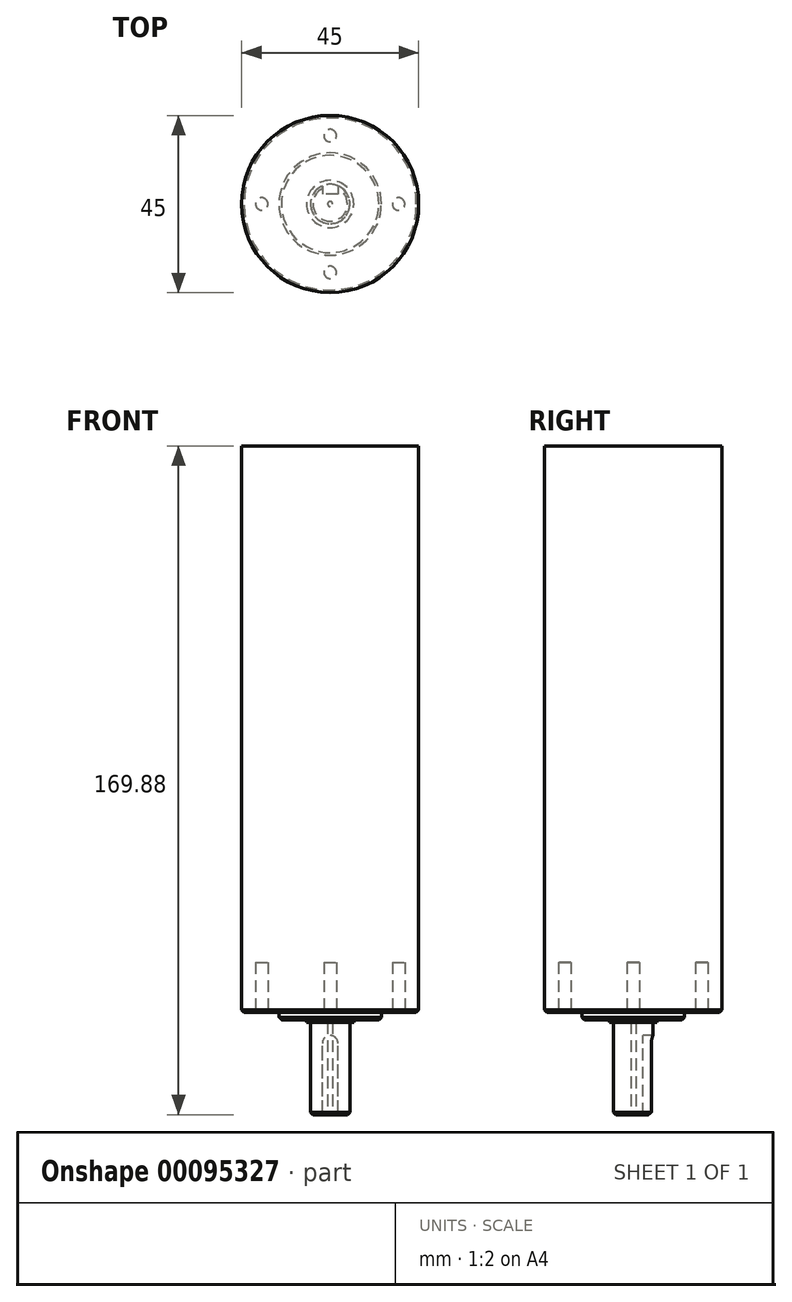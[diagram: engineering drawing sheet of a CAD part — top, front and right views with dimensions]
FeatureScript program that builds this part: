
annotation { "Feature Type Name" : "Feature", "Feature Type Description" : "" }
export const myFeature = defineFeature(function(context is Context, id is Id, definition is map)
    precondition{}
    {
        {
            var Q0;
            Q0=qCreatedBy(makeId("Top.planeOp"),FACE);
            var sketch = newSketch(context, id + "F0", { "sketchPlane" : qUnion([Q0])});
            skCircle(sketch, "E0", {"center": v(0, 0) * mm, "radius": 22.5 * mm});
            skSolve(sketch);
        }
        {
            var Q0;
            Q0=makeQuery(id+"F0.imprint","IMPRINT",FACE,{"disambiguationData":[TD([[makeQuery(id+"F0.imprint","IMPRINT",EDGE,{"derivedFrom":sQuery(id+"F0.wireOp",EDGE,"E0")}),1.0]])]});
            extrude(context, id + "F1", {"entities" : qUnion([Q0]), "oppositeDirection" : true, "depth" : 143.84 * mm});
        }
        {
            var Q0;
            Q0=makeQuery(id+"F1.opExtrude","CAP_FACE",FACE,{"disambiguationData":[OSD([sQuery(id+"F0.wireOp",EDGE,"E0")])],"isStart":false});
            var sketch = newSketch(context, id + "F2", { "sketchPlane" : qUnion([Q0])});
            skCircle(sketch, "E1", {"center": v(0, 0) * mm, "radius": 13 * mm});
            skSolve(sketch);
        }
        {
            var Q0;
            Q0=makeQuery(id+"F2.imprint","IMPRINT",FACE,{"disambiguationData":[TD([[makeQuery(id+"F2.imprint","IMPRINT",EDGE,{"derivedFrom":sQuery(id+"F2.wireOp",EDGE,"E1")}),1.0]])]});
            extrude(context, id + "F3", {"entities" : qUnion([Q0]), "operationType" : NewBodyOperationType.ADD, "depth" : 1.9 * mm});
        }
        {
            var Q0;
            Q0=makeQuery(id+"F3.opExtrude","CAP_FACE",FACE,{"disambiguationData":[OSD([sQuery(id+"F2.wireOp",EDGE,"E1")])],"isStart":false});
            var sketch = newSketch(context, id + "F4", { "sketchPlane" : qUnion([Q0])});
            skCircle(sketch, "E2", {"center": v(0, 0) * mm, "radius": 6 * mm});
            skSolve(sketch);
        }
        {
            var Q0;
            Q0=makeQuery(id+"F4.imprint","IMPRINT",FACE,{"disambiguationData":[TD([[makeQuery(id+"F4.imprint","IMPRINT",EDGE,{"derivedFrom":sQuery(id+"F4.wireOp",EDGE,"E2")}),1.0]])]});
            extrude(context, id + "F5", {"entities" : qUnion([Q0]), "operationType" : NewBodyOperationType.ADD, "depth" : 0.64 * mm});
        }
        {
            var Q0;
            Q0=makeQuery(id+"F5.opExtrude","CAP_FACE",FACE,{"disambiguationData":[OSD([sQuery(id+"F4.wireOp",EDGE,"E2")])],"isStart":false});
            var sketch = newSketch(context, id + "F6", { "sketchPlane" : qUnion([Q0])});
            skCircle(sketch, "E3", {"center": v(0, 0) * mm, "radius": 5 * mm});
            skSolve(sketch);
        }
        {
            var Q0;
            Q0=makeQuery(id+"F6.imprint","IMPRINT",FACE,{"disambiguationData":[TD([[makeQuery(id+"F6.imprint","IMPRINT",EDGE,{"derivedFrom":sQuery(id+"F6.wireOp",EDGE,"E3")}),1.0]])]});
            extrude(context, id + "F7", {"entities" : qUnion([Q0]), "operationType" : NewBodyOperationType.ADD, "depth" : 23.5 * mm});
        }
        {
            var Q0;
            Q0=qCreatedBy(makeId("Front.planeOp"),FACE);
            cPlane(context, id + "F8", {"entities" : qUnion([Q0]), "cplaneType" : CPlaneType.OFFSET, "offset" : 2.45 * mm, "oppositeDirection" : true, "width" : 152.4 * mm, "height" : 152.4 * mm});
        }
        {
            var Q0;
            Q0=qCreatedBy(id+"F8.planeOp",FACE);
            var sketch = newSketch(context, id + "F9", { "sketchPlane" : qUnion([Q0])});
            skLineSegment(sketch, "E4", {"start": v(5, -146.38) * mm, "end": v(5, -169.88) * mm, "construction": true});
            skLineSegment(sketch, "E5", {"start": v(-5, -169.88) * mm, "end": v(-5, -146.38) * mm, "construction": true});
            skLineSegment(sketch, "E6", {"start": v(0, -169.88) * mm, "end": v(-1.98, -169.88) * mm});
            skLineSegment(sketch, "E7", {"start": v(-1.98, -169.88) * mm, "end": v(-1.98, -151.74) * mm});
            skLineSegment(sketch, "E8", {"start": v(0, -169.88) * mm, "end": v(0, -146.38) * mm, "construction": true});
            skLineSegment(sketch, "E9.MirrorCS", {"start": v(1.98, -169.88) * mm, "end": v(1.98, -151.74) * mm});
            skLineSegment(sketch, "E10.MirrorCS", {"start": v(0, -169.88) * mm, "end": v(1.98, -169.88) * mm});
            skArc(sketch, "E11", {"start": v(1.98, -151.74) * mm, "mid": v(0, -149.76) * mm, "end": v(-1.98, -151.74) * mm});
            skSolve(sketch);
        }
        {
            var Q0;
            Q0 = qSketchRegion(id + "F9", true);
            extrude(context, id + "F10", {"entities" : qUnion([Q0]), "operationType" : NewBodyOperationType.REMOVE, "endBound" : BoundingType.THROUGH_ALL, "oppositeDirection" : true, "depth" : 25.4 * mm});
        }
        {
            var Q0;
            Q0=makeQuery(id+"F7.opExtrude","CAP_FACE",FACE,{"disambiguationData":[OSD([sQuery(id+"F6.wireOp",EDGE,"E3")])],"isStart":false});
            var sketch = newSketch(context, id + "F11", { "sketchPlane" : qUnion([Q0])});
            skCircle(sketch, "E12", {"center": v(0, 0) * mm, "radius": 0.64 * mm});
            skSolve(sketch);
        }
        {
            var Q0;
            Q0=makeQuery(id+"F11.imprint","IMPRINT",FACE,{"disambiguationData":[TD([[makeQuery(id+"F11.imprint","IMPRINT",EDGE,{"derivedFrom":sQuery(id+"F11.wireOp",EDGE,"E12")}),1.0]])]});
            extrude(context, id + "F12", {"entities" : qUnion([Q0]), "operationType" : NewBodyOperationType.REMOVE, "oppositeDirection" : true, "depth" : 23.5 * mm});
        }
        {
            var Q0;
            Q0=makeQuery(id+"F1.opExtrude","CAP_FACE",FACE,{"disambiguationData":[OSD([sQuery(id+"F0.wireOp",EDGE,"E0")])],"isStart":false});
            var sketch = newSketch(context, id + "F13", { "sketchPlane" : qUnion([Q0])});
            skLineSegment(sketch, "E13", {"start": v(0, 0) * mm, "end": v(0, 22.5) * mm, "construction": true});
            skCircle(sketch, "E14", {"center": v(0, 17.38) * mm, "radius": 1.59 * mm});
            skCircle(sketch, "E15.1.0", {"center": v(-17.38, 0) * mm, "radius": 1.59 * mm});
            skCircle(sketch, "E15.2.0", {"center": v(0, -17.38) * mm, "radius": 1.59 * mm});
            skCircle(sketch, "E15.3.0", {"center": v(17.38, 0) * mm, "radius": 1.59 * mm});
            skPoint(sketch, "E15.center", {"position": v(0, 0) * mm});
            skSolve(sketch);
        }
        {
            var Q0;
            Q0 = qSketchRegion(id + "F13", true);
            extrude(context, id + "F14", {"entities" : qUnion([Q0]), "operationType" : NewBodyOperationType.REMOVE, "oppositeDirection" : true, "depth" : 12.7 * mm});
        }
        {
            var Q0;
            Q0=makeQuery(id+"F12.boolean.opBoolean","COPY",EDGE,{"derivedFrom":makeQuery(id+"F12.opExtrude","CAP_EDGE",EDGE,{"disambiguationData":[OSD([sQuery(id+"F11.wireOp",EDGE,"E12")])],"isStart":true})});
            var Q1;
            Q1=makeQuery(id+"F14.boolean.opBoolean","COPY",EDGE,{"derivedFrom":makeQuery(id+"F14.opExtrude","CAP_EDGE",EDGE,{"disambiguationData":[OSD([sQuery(id+"F13.wireOp",EDGE,"E15.1.0")])],"isStart":true})});
            var Q2;
            Q2=makeQuery(id+"F14.boolean.opBoolean","COPY",EDGE,{"derivedFrom":makeQuery(id+"F14.opExtrude","CAP_EDGE",EDGE,{"disambiguationData":[OSD([sQuery(id+"F13.wireOp",EDGE,"E15.2.0")])],"isStart":true})});
            var Q3;
            Q3=makeQuery(id+"F14.boolean.opBoolean","COPY",EDGE,{"derivedFrom":makeQuery(id+"F14.opExtrude","CAP_EDGE",EDGE,{"disambiguationData":[OSD([sQuery(id+"F13.wireOp",EDGE,"E15.3.0")])],"isStart":true})});
            var Q4;
            Q4=makeQuery(id+"F14.boolean.opBoolean","COPY",EDGE,{"derivedFrom":makeQuery(id+"F14.opExtrude","CAP_EDGE",EDGE,{"disambiguationData":[OSD([sQuery(id+"F13.wireOp",EDGE,"E14")])],"isStart":true})});
            var Q5;
            Q5=makeQuery(id+"F7.opExtrude","CAP_EDGE",EDGE,{"disambiguationData":[OSD([sQuery(id+"F6.wireOp",EDGE,"E3")])],"isStart":false});
            var Q6;
            Q6=makeQuery(id+"F3.opExtrude","CAP_EDGE",EDGE,{"disambiguationData":[OSD([sQuery(id+"F2.wireOp",EDGE,"E1")])],"isStart":false});
            var Q7;
            Q7=makeQuery(id+"F1.opExtrude","CAP_EDGE",EDGE,{"disambiguationData":[OSD([sQuery(id+"F0.wireOp",EDGE,"E0")])],"isStart":false});
            chamfer(context, id + "F15", {"entities" : qUnion([Q0, Q1, Q2, Q3, Q4, Q5, Q6, Q7]), "width" : 0.64 * mm, "tangentPropagation" : true});
        }
    });
